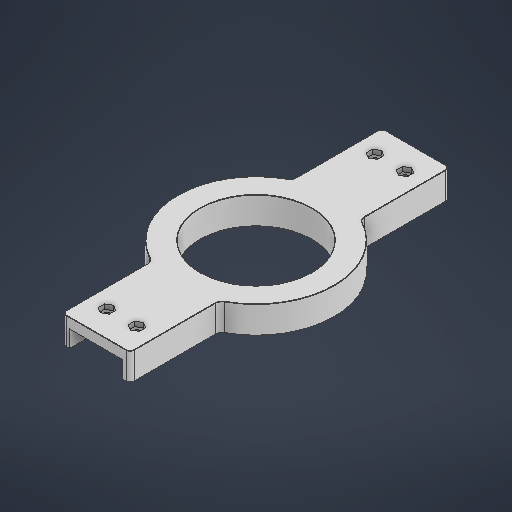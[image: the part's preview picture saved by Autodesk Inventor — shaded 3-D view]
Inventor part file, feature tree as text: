
AUTODESK INVENTOR PART (.ipt)
format: ipt  version: 2025 (Build 290162000, 162)  size: 391,168 bytes
history: native  units: in
note: dims shown in document units (in); Inventor stores cm internally (conversion verified against a paired STEP export)
features: sketch x6, extrude x4, fillet x2, chamfer x1, hole x1
ambient origin geometry x8: Origin, YZ Plane, XZ Plane, XY Plane, X Axis, Y Axis, Z Axis, Center Point
bodies: Solid1 (feature_tree)
feature tree (14):
  extrude  "Extrusion1"  Depth=0.1969in
  fillet  "Fillet1"  Radius=0.7874in
  fillet  "Fillet2"  Radius=0.1969in
  chamfer  "Chamfer1"  Distance=0.0098in Angle=45.0deg
  extrude  "Extrusion4"  Depth=1.5453in
  hole  "Hole2"  [1 undecoded]
  extrude  "Extrusion5"  Depth=0.1181in
  extrude  "Extrusion6"  Depth=0.4951in TaperAngle=0.0deg
  sketch  "Sketch1"  dims[d0=3.2283in d3=4.5276in d4=0.7874in d5=0.0in d28=0.1969in]
  sketch  "Sketch3"  dims[d29=0.1181in d30=0.0098in d31=0.0787in d32=45.0deg]
  sketch  "Sketch4"  dims[d38=1.1122in d39=1.5453in]
  sketch  "Sketch5"  dims[d40=0.1181in d41=0.1181in]
  sketch  "Sketch6"  dims[d42=0.1181in d43=0.4951in d44=0.0in d45=0.748in d48=0.748in d50=0.0935in d51=0.0935in d52=1.7323in d53=1.5453in d55=0.0935in d56=0.0935in d57=0.748in d58=0.748in d59=0.8661in d60=0.8661in d61=0.3396in d62=0.3396in d63=0.1628in d64=0.3937in d65=0.1575in d66=0.0787in d67=90.0deg d68=0.315in d69=0.8108in d70=0.3248in d71=0.3248in d72=0.3248in d73=0.3248in d74=0.1358in d75=0.0in d76=1.9685in d77=2.2638in d78=2.2638in d79=2.5874in d80=2.5874in d81=1.9685in d82=9.252in d83=9.2323in d84=3.7402in d85=0.2756in d86=3.1496in d88=360.0deg d90=0.2756in d91=0.0in d46=0.0344in]
  sketch  "Sketch Circular Pattern3"  dims[d35=1.5453in d37=1.1122in]
note: 1 required parameter value undecoded (feature->parameter linkage not recoverable at this tier; creation-order binding heuristic only, values carry confidence <= 0.55)
